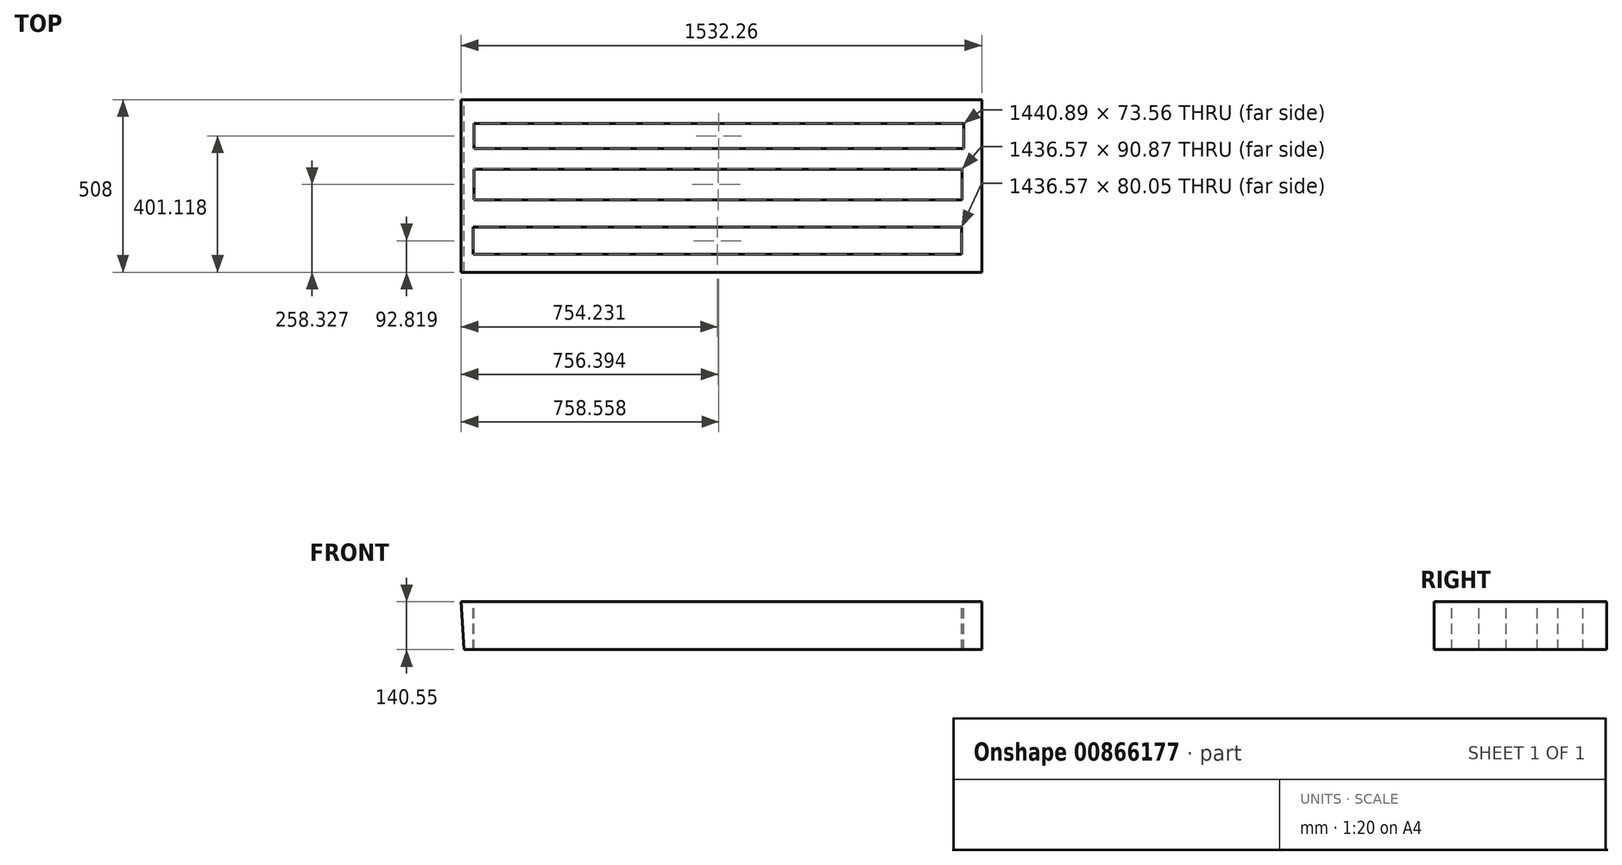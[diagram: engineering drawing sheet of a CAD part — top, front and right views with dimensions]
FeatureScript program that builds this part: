
annotation { "Feature Type Name" : "Feature", "Feature Type Description" : "" }
export const myFeature = defineFeature(function(context is Context, id is Id, definition is map)
    precondition{}
    {
        {
            var Q0;
            Q0=qCreatedBy(makeId("Front.planeOp"),FACE);
            var sketch = newSketch(context, id + "F0", { "sketchPlane" : qUnion([Q0])});
            skLineSegment(sketch, "E0", {"start": v(-773.18, 116.44) * mm, "end": v(759.08, 116.44) * mm});
            skLineSegment(sketch, "E1", {"start": v(759.08, 116.44) * mm, "end": v(759.08, -24.11) * mm});
            skLineSegment(sketch, "E2", {"start": v(759.08, -24.11) * mm, "end": v(-764.92, -24.11) * mm});
            skLineSegment(sketch, "E3", {"start": v(-764.92, -24.11) * mm, "end": v(-773.18, 116.44) * mm});
            skSolve(sketch);
        }
        {
            var Q0;
            Q0 = qSketchRegion(id + "F0", true);
            extrude(context, id + "F1", {"entities" : qUnion([Q0]), "depth" : 508 * mm, "offsetDistance" : 25.4 * mm});
        }
        {
            var Q0;
            Q0=makeQuery(id+"F1.opExtrude","SWEPT_FACE",FACE,{"disambiguationData":[OSD([sQuery(id+"F0.wireOp",EDGE,"E0")])]});
            var sketch = newSketch(context, id + "F2", { "sketchPlane" : qUnion([Q0])});
            skLineSegment(sketch, "E4.bottom", {"start": v(699.33, -455.2) * mm, "end": v(-737.23, -455.2) * mm});
            skLineSegment(sketch, "E4.top", {"start": v(699.33, -375.16) * mm, "end": v(-737.23, -375.16) * mm});
            skLineSegment(sketch, "E4.left", {"start": v(699.33, -455.2) * mm, "end": v(699.33, -375.16) * mm});
            skLineSegment(sketch, "E4.right", {"start": v(-737.23, -455.2) * mm, "end": v(-737.23, -375.16) * mm});
            skLineSegment(sketch, "E5.bottom", {"start": v(701.5, -295.1) * mm, "end": v(-735.07, -295.1) * mm});
            skLineSegment(sketch, "E5.top", {"start": v(701.5, -204.24) * mm, "end": v(-735.07, -204.24) * mm});
            skLineSegment(sketch, "E5.left", {"start": v(701.5, -295.1) * mm, "end": v(701.5, -204.24) * mm});
            skLineSegment(sketch, "E5.right", {"start": v(-735.07, -295.1) * mm, "end": v(-735.07, -204.24) * mm});
            skPoint(sketch, "E6.oppositeSnap0", {"position": v(-735.07, -249.67) * mm});
            skLineSegment(sketch, "E6.bottom", {"start": v(705.82, -143.66) * mm, "end": v(-735.07, -143.66) * mm});
            skLineSegment(sketch, "E6.top", {"start": v(705.82, -70.1) * mm, "end": v(-735.07, -70.1) * mm});
            skLineSegment(sketch, "E6.left", {"start": v(705.82, -143.66) * mm, "end": v(705.82, -70.1) * mm});
            skLineSegment(sketch, "E6.right", {"start": v(-735.07, -143.66) * mm, "end": v(-735.07, -70.1) * mm});
            skSolve(sketch);
        }
        {
            var Q0;
            Q0 = qSketchRegion(id + "F2", true);
            extrude(context, id + "F3", {"entities" : qUnion([Q0]), "operationType" : NewBodyOperationType.REMOVE, "oppositeDirection" : true, "depth" : 254 * mm, "offsetDistance" : 25.4 * mm});
        }
    });
